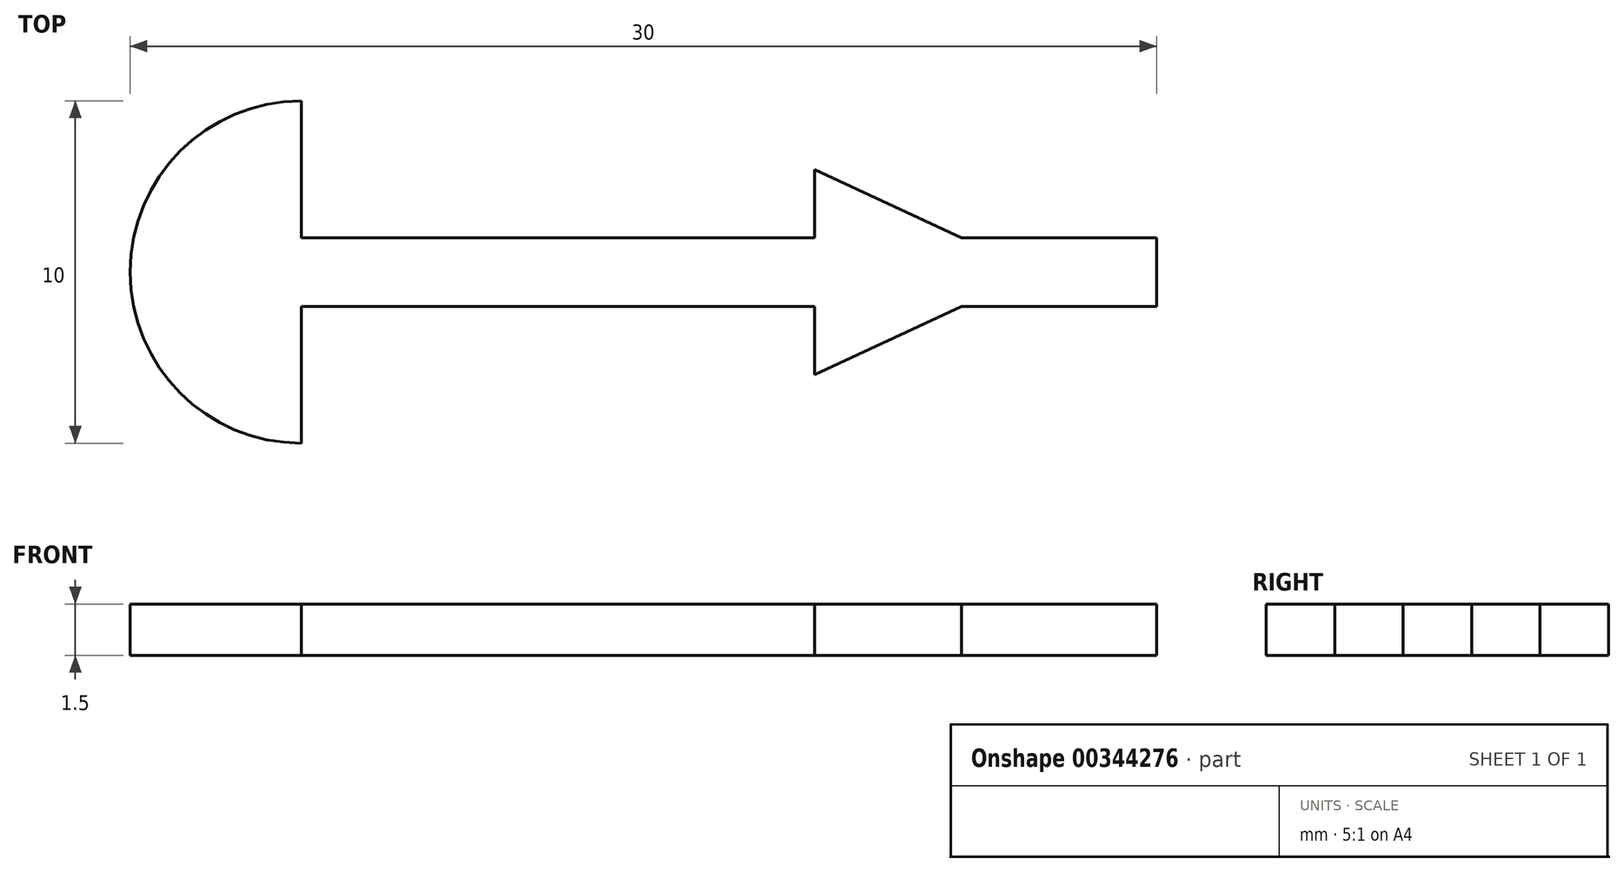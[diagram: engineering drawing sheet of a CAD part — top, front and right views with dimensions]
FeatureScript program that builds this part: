
annotation { "Feature Type Name" : "Feature", "Feature Type Description" : "" }
export const myFeature = defineFeature(function(context is Context, id is Id, definition is map)
    precondition{}
    {
        {
            var Q0;
            Q0=qCreatedBy(makeId("Top.planeOp"),FACE);
            var sketch = newSketch(context, id + "F0", { "sketchPlane" : qUnion([Q0])});
            skLineSegment(sketch, "E0.bottom", {"start": v(0, 1) * mm, "end": v(25, 1) * mm});
            skLineSegment(sketch, "E0.top", {"start": v(0, -1) * mm, "end": v(25, -1) * mm});
            skLineSegment(sketch, "E0.left", {"start": v(0, 1) * mm, "end": v(0, -1) * mm});
            skLineSegment(sketch, "E0.right", {"start": v(25, 1) * mm, "end": v(25, -1) * mm});
            skLineSegment(sketch, "E1", {"start": v(0, 5) * mm, "end": v(0, -5) * mm});
            skLineSegment(sketch, "E2", {"start": v(0, 0) * mm, "end": v(25, 0) * mm, "construction": true});
            skArc(sketch, "E3", {"start": v(0, 5) * mm, "mid": v(-5, 0) * mm, "end": v(0, -5) * mm});
            skLineSegment(sketch, "E4", {"start": v(15, -1) * mm, "end": v(15, -3) * mm});
            skLineSegment(sketch, "E5", {"start": v(15, -3) * mm, "end": v(19.29, -1) * mm});
            skLineSegment(sketch, "E6.MirrorCS", {"start": v(15, 1) * mm, "end": v(15, 3) * mm});
            skLineSegment(sketch, "E7.MirrorCS", {"start": v(15, 3) * mm, "end": v(19.29, 1) * mm});
            skSolve(sketch);
        }
        {
            var Q0;
            Q0 = qSketchRegion(id + "F0", true);
            extrude(context, id + "F1", {"entities" : qUnion([Q0]), "depth" : 1.5 * mm});
        }
    });
